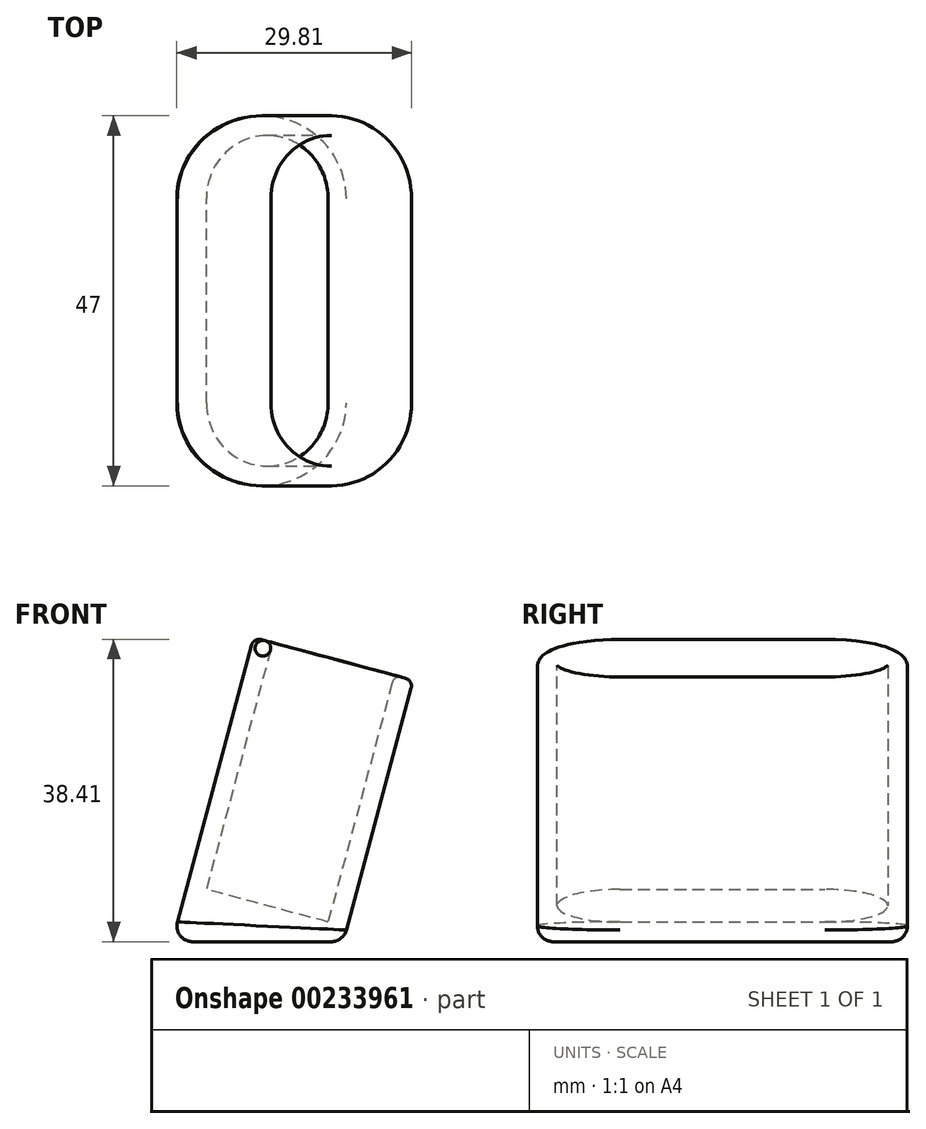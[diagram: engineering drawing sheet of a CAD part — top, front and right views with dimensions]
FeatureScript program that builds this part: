
annotation { "Feature Type Name" : "Feature", "Feature Type Description" : "" }
export const myFeature = defineFeature(function(context is Context, id is Id, definition is map)
    precondition{}
    {
        {
            assignVariable(context, id + "F0", {"name" : "Width", "anyValue" : 21});
        }
        {
            assignVariable(context, id + "F1", {"name" : "Height", "anyValue" : 40});
        }
        {
            assignVariable(context, id + "F2", {"name" : "Wall", "anyValue" : 2.5});
        }
        {
            var Q0;
            Q0=qCreatedBy(makeId("Top.planeOp"),FACE);
            var sketch = newSketch(context, id + "F3", { "sketchPlane" : qUnion([Q0])});
            skLineSegment(sketch, "E0", {"start": v(0, -250) * mm, "end": v(0, 250) * mm, "construction": true});
            skSolve(sketch);
        }
        {
            var Q0;
            Q0=sQuery(id+"F3.wireOp",EDGE,"E0");
            var Q1;
            Q1=qCreatedBy(makeId("Top.planeOp"),FACE);
            cPlane(context, id + "F4", {"entities" : qUnion([Q0, Q1]), "cplaneType" : CPlaneType.LINE_ANGLE, "offset" : 25 * mm, "angle" : 15 * degree, "width" : 150 * mm, "height" : 150 * mm});
        }
        {
            var Q0;
            Q0=qCreatedBy(id+"F4.planeOp",FACE);
            var sketch = newSketch(context, id + "F5", { "sketchPlane" : qUnion([Q0])});
            skLineSegment(sketch, "E1.bottom", {"start": v(10.5, -23.5) * mm, "end": v(-10.5, -23.5) * mm});
            skLineSegment(sketch, "E1.top", {"start": v(10.5, 23.5) * mm, "end": v(-10.5, 23.5) * mm});
            skLineSegment(sketch, "E1.left", {"start": v(10.5, -23.5) * mm, "end": v(10.5, 23.5) * mm});
            skLineSegment(sketch, "E1.right", {"start": v(-10.5, -23.5) * mm, "end": v(-10.5, 23.5) * mm});
            skPoint(sketch, "E1.middle", {"position": v(0, 0) * mm});
            skSolve(sketch);
        }
        {
            var Q0;
            Q0 = qSketchRegion(id + "F5", true);
            extrude(context, id + "F6", {"entities" : qUnion([Q0]), "oppositeDirection" : true, "depth" : (getVariable(context, 'Height')) * mm});
        }
        {
            var Q0;
            Q0=makeQuery(id+"F6.opExtrude","SWEPT_FACE",FACE,{"disambiguationData":[OSD([sQuery(id+"F5.wireOp",EDGE,"E1.top")])]});
            var sketch = newSketch(context, id + "F7", { "sketchPlane" : qUnion([Q0])});
            skLineSegment(sketch, "E2", {"start": v(-10.14, 2.72) * mm, "end": v(11.6, 2.72) * mm});
            skLineSegment(sketch, "E3", {"start": v(11.6, 2.72) * mm, "end": v(10.14, -2.72) * mm});
            skLineSegment(sketch, "E4", {"start": v(10.14, -2.72) * mm, "end": v(-10.14, 2.72) * mm});
            skSolve(sketch);
        }
        {
            var Q0;
            Q0 = qSketchRegion(id + "F7", true);
            extrude(context, id + "F8", {"entities" : qUnion([Q0]), "operationType" : NewBodyOperationType.REMOVE, "endBound" : BoundingType.THROUGH_ALL, "oppositeDirection" : true, "depth" : 25 * mm});
        }
        {
            var Q0;
            Q0=makeQuery(id+"F6.opExtrude","SWEPT_EDGE",EDGE,{"disambiguationData":[OSD([sQuery(id+"F5.wireOp",EDGE,"E1.top"),sQuery(id+"F5.wireOp",EDGE,"E1.right")])]});
            var Q1;
            Q1=makeQuery(id+"F6.opExtrude","SWEPT_EDGE",EDGE,{"disambiguationData":[OSD([sQuery(id+"F5.wireOp",EDGE,"E1.top"),sQuery(id+"F5.wireOp",EDGE,"E1.left")])]});
            var Q2;
            Q2=makeQuery(id+"F6.opExtrude","SWEPT_EDGE",EDGE,{"disambiguationData":[OSD([sQuery(id+"F5.wireOp",EDGE,"E1.bottom"),sQuery(id+"F5.wireOp",EDGE,"E1.right")])]});
            var Q3;
            Q3=makeQuery(id+"F6.opExtrude","SWEPT_EDGE",EDGE,{"disambiguationData":[OSD([sQuery(id+"F5.wireOp",EDGE,"E1.bottom"),sQuery(id+"F5.wireOp",EDGE,"E1.left")])]});
            fillet(context, id + "F9", {"entities" : qUnion([Q0, Q1, Q2, Q3]), "radius" : (getVariable(context, 'Width') / 2) * mm, "tangentPropagation" : true, "allowEdgeOverflow" : false});
        }
        {
            var Q0;
            Q0=makeQuery(id+"F9.opFillet","BLEND_EDGE",EDGE,{"blendedFrom":[makeQuery(id+"F6.opExtrude","SWEPT_EDGE",EDGE,{"disambiguationData":[OSD([sQuery(id+"F5.wireOp",EDGE,"E1.top"),sQuery(id+"F5.wireOp",EDGE,"E1.right")])]}),makeQuery(id+"F8.boolean.opBoolean","COPY",FACE,{"derivedFrom":makeQuery(id+"F8.opExtrude","SWEPT_FACE",FACE,{"disambiguationData":[OSD([sQuery(id+"F7.wireOp",EDGE,"E2")])]})})],"blendedInto":[makeQuery(id+"F8.boolean.opBoolean","COPY",FACE,{"derivedFrom":makeQuery(id+"F8.opExtrude","SWEPT_FACE",FACE,{"disambiguationData":[OSD([sQuery(id+"F7.wireOp",EDGE,"E2")])]})})]});
            fillet(context, id + "F10", {"entities" : qUnion([Q0]), "radius" : 2 * mm, "tangentPropagation" : true, "allowEdgeOverflow" : false});
        }
        {
            var Q0;
            Q0=makeQuery(id+"F6.opExtrude","CAP_FACE",FACE,{"disambiguationData":[OSD([sQuery(id+"F5.wireOp",EDGE,"E1.bottom"),sQuery(id+"F5.wireOp",EDGE,"E1.top"),sQuery(id+"F5.wireOp",EDGE,"E1.left"),sQuery(id+"F5.wireOp",EDGE,"E1.right")])],"isStart":false});
            shell(context, id + "F11", {"entities" : qUnion([Q0]), "thickness" : (getVariable(context, 'Wall')) * mm});
        }
        {
            var Q0;
            Q0=qCreatedBy(makeId("Front.planeOp"),FACE);
            var sketch = newSketch(context, id + "F12", { "sketchPlane" : qUnion([Q0])});
            skLineSegment(sketch, "E5.0", {"start": v(-6.88, 5.22) * mm, "end": v(9.68, 5.22) * mm});
            skLineSegment(sketch, "E6", {"start": v(-6.88, 5.22) * mm, "end": v(-5.77, 9.36) * mm});
            skLineSegment(sketch, "E7", {"start": v(-5.77, 9.36) * mm, "end": v(9.68, 5.22) * mm});
            skSolve(sketch);
        }
        {
            var Q0;
            Q0 = qSketchRegion(id + "F12", true);
            extrude(context, id + "F13", {"entities" : qUnion([Q0]), "operationType" : NewBodyOperationType.ADD, "endBound" : BoundingType.UP_TO_NEXT, "depth" : 25 * mm, "offsetDistance" : 25 * mm, "hasSecondDirection" : true, "secondDirectionBound" : BoundingType.UP_TO_NEXT, "secondDirectionOppositeDirection" : true, "secondDirectionDepth" : 25 * mm});
        }
        {
            var Q0;
            Q0=makeQuery(id+"F11.opShell","OFFSET_EDGE",EDGE,{"disambiguationData":[OSD([sQuery(id+"F5.wireOp",EDGE,"E1.right")])]});
            var Q1;
            Q1=makeQuery(id+"F6.opExtrude","CAP_EDGE",EDGE,{"disambiguationData":[OSD([sQuery(id+"F5.wireOp",EDGE,"E1.right")])],"isStart":false});
            fillet(context, id + "F14", {"entities" : qUnion([Q0, Q1]), "radius" : 1 * mm, "tangentPropagation" : true, "allowEdgeOverflow" : false});
        }
    });
